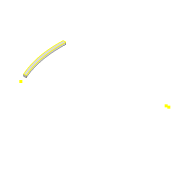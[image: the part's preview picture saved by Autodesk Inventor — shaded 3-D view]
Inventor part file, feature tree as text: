
AUTODESK INVENTOR PART (.ipt)
format: ipt  version: 2022 (Build 260153000, 153)  size: 123,392 bytes
history: native  units: mm
features: sketch x4, extrude x2, projected_geometry x2, fillet x1
ambient origin geometry x8: Origin, YZ Plane, XZ Plane, XY Plane, X Axis, Y Axis, Z Axis, Center Point
bodies: Solid1 (feature_tree)
feature tree (9):
  extrude  "Extrusion1"  Depth=10.0mm
  fillet  "Fillet1"  Radius=3.0mm
  sketch  "Sketch2"  dims[d3=3.0mm d4=8.0mm d5=0.0mm]
  extrude  "Extrusion2"  Depth=8.0mm TaperAngle=0.0deg
  sketch  "Sketch4"  dims[d13=400.0mm d14=2.0mm d15=30.0mm d16=180.0mm d17=190.354919mm d18=20.0mm d19=0.0mm]
  sketch  "Sketch1"  dims[d0=382.775mm d1=10.0mm d2=3.0mm]
  projected_geometry  "Projected Loop1"
  sketch  "Sketch3"  dims[d12=400.0mm]
  projected_geometry  "Projected Loop2"
